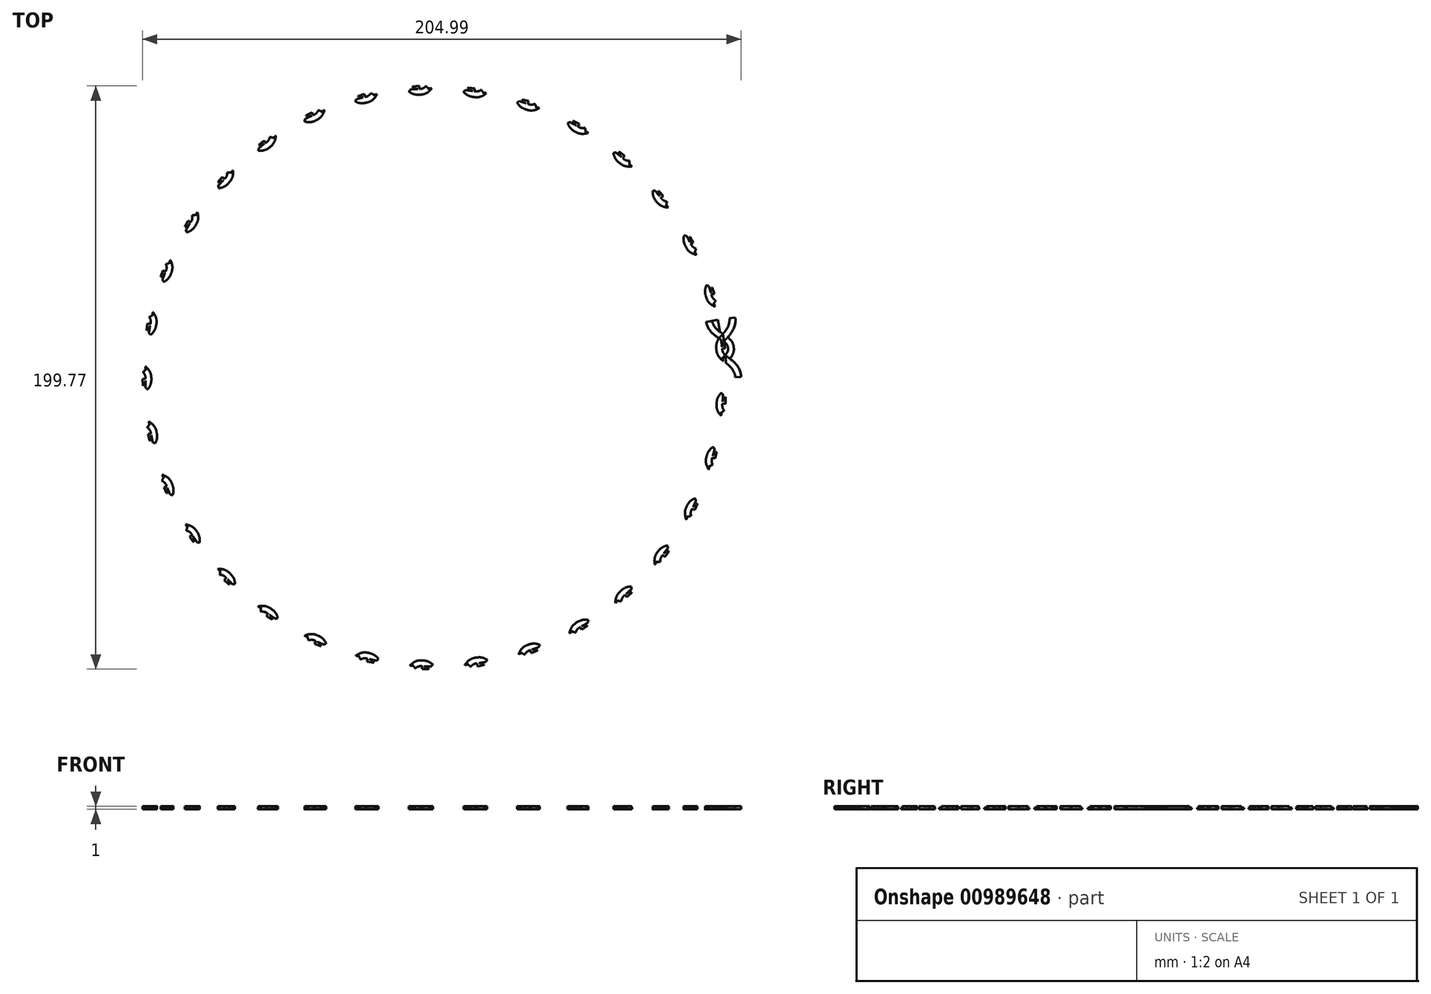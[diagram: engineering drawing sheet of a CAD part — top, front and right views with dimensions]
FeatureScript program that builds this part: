
annotation { "Feature Type Name" : "Feature", "Feature Type Description" : "" }
export const myFeature = defineFeature(function(context is Context, id is Id, definition is map)
    precondition{}
    {
        {
            var Q0;
            Q0=qCreatedBy(makeId("Top.planeOp"),FACE);
            var sketch = newSketch(context, id + "F0", { "sketchPlane" : qUnion([Q0])});
            skCircle(sketch, "E0.0", {"center": v(0.06, -0.4) * mm, "radius": 101 * mm});
            skCircle(sketch, "E1.0", {"center": v(0, 0) * mm, "radius": 99 * mm});
            skLineSegment(sketch, "E2", {"start": v(100, 0) * mm, "end": v(99.75, 5) * mm});
            skLineSegment(sketch, "E3", {"start": v(100, 0) * mm, "end": v(97, -0.15) * mm});
            skLineSegment(sketch, "E4", {"start": v(100, 0) * mm, "end": v(103, 0.15) * mm});
            skLineSegment(sketch, "E5", {"start": v(99.5, 9.99) * mm, "end": v(96.52, 9.69) * mm});
            skLineSegment(sketch, "E6", {"start": v(99.5, 9.99) * mm, "end": v(102.49, 10.29) * mm});
            skFitSpline(sketch, "E7", {"points": [v(102.49, 10.29) * mm, v(99.75, 5) * mm, v(97, -0.15) * mm], "startDerivative": vector(1.73, -14.4) * mm, "endDerivative": vector(0.3, -13.17) * mm});
            skLineSegment(sketch, "E8", {"start": v(99.5, 9.99) * mm, "end": v(100, 0) * mm});
            skPoint(sketch, "E9", {"position": v(99.6, 7.89) * mm});
            skPoint(sketch, "E10", {"position": v(99.89, 2.2) * mm});
            skLineSegment(sketch, "E11", {"start": v(99.75, 5) * mm, "end": v(99.5, 9.99) * mm});
            skFitSpline(sketch, "E12.0", {"points": [v(100.5, 10.05) * mm, v(100.52, 9.86) * mm, v(100.53, 9.55) * mm, v(100.46, 9.15) * mm, v(100.33, 8.78) * mm, v(100.11, 8.38) * mm, v(99.8, 7.95) * mm, v(99.4, 7.48) * mm, v(98.9, 6.98) * mm, v(98.36, 6.44) * mm, v(97.79, 5.85) * mm, v(97.02, 5.02) * mm, v(96.27, 4.06) * mm, v(95.65, 2.92) * mm, v(95.15, 1.66) * mm, v(94.99, 0.57) * mm, v(95, -0.2) * mm]});
            skFitSpline(sketch, "E13", {"points": [v(96.52, 9.69) * mm, v(99.75, 5) * mm, v(103, 0.15) * mm], "startDerivative": vector(1.05, -15.9) * mm, "endDerivative": vector(1.59, -14.28) * mm});
            skFitSpline(sketch, "E14.0", {"points": [v(98.51, 9.82) * mm, v(98.53, 9.58) * mm, v(98.59, 9.18) * mm, v(98.73, 8.73) * mm, v(98.91, 8.38) * mm, v(99.15, 8.06) * mm, v(99.47, 7.73) * mm, v(99.88, 7.39) * mm, v(100.38, 7) * mm, v(100.97, 6.59) * mm, v(101.59, 6.1) * mm, v(102.22, 5.57) * mm, v(102.85, 4.96) * mm, v(103.66, 4.03) * mm, v(104.52, 2.58) * mm, v(104.9, 1.14) * mm, v(104.98, 0.37) * mm]});
            skFitSpline(sketch, "E15.MirrorCS", {"points": [v(96.52, 9.69) * mm, v(98.75, 14.93) * mm, v(100.97, 20.32) * mm], "startDerivative": vector(-2.13, 15.8) * mm, "endDerivative": vector(-1.28, 14.3) * mm});
            skFitSpline(sketch, "E16.MirrorCS", {"points": [v(102.49, 10.29) * mm, v(98.75, 14.93) * mm, v(95.04, 19.43) * mm], "startDerivative": vector(-1.17, 14.46) * mm, "endDerivative": vector(-2.33, 12.96) * mm});
            skFitSpline(sketch, "E17.0", {"points": [v(100.5, 10.13) * mm, v(100.48, 10.31) * mm, v(100.42, 10.62) * mm, v(100.28, 11) * mm, v(100.07, 11.34) * mm, v(99.78, 11.68) * mm, v(99.39, 12.05) * mm, v(98.9, 12.42) * mm, v(98.32, 12.82) * mm, v(97.68, 13.24) * mm, v(97, 13.7) * mm, v(96.08, 14.37) * mm, v(95.16, 15.15) * mm, v(94.32, 16.14) * mm, v(93.58, 17.29) * mm, v(93.2, 18.32) * mm, v(93.07, 19.07) * mm]});
            skFitSpline(sketch, "E18.0", {"points": [v(98.5, 9.96) * mm, v(98.47, 10.2) * mm, v(98.44, 10.6) * mm, v(98.5, 11.06) * mm, v(98.6, 11.44) * mm, v(98.77, 11.8) * mm, v(99.02, 12.19) * mm, v(99.36, 12.61) * mm, v(99.77, 13.08) * mm, v(100.26, 13.61) * mm, v(100.78, 14.2) * mm, v(101.3, 14.85) * mm, v(101.79, 15.58) * mm, v(102.39, 16.66) * mm, v(102.95, 18.24) * mm, v(103.03, 19.73) * mm, v(102.96, 20.5) * mm]});
            skLineSegment(sketch, "E19", {"start": v(97, -0.15) * mm, "end": v(95, -0.25) * mm});
            skLineSegment(sketch, "E20", {"start": v(103, 0.15) * mm, "end": v(105, 0.25) * mm});
            skLineSegment(sketch, "E21", {"start": v(95, 0.02) * mm, "end": v(95, -0.25) * mm});
            skLineSegment(sketch, "E22", {"start": v(104.98, 0.37) * mm, "end": v(105, 0.25) * mm});
            skCircle(sketch, "E23", {"center": v(0.06, -0.4) * mm, "radius": 100 * mm, "construction": true});
            skLineSegment(sketch, "E24", {"start": v(99.5, 9.99) * mm, "end": v(97.99, 19.87) * mm});
            skLineSegment(sketch, "E25", {"start": v(100.97, 20.32) * mm, "end": v(95.04, 19.43) * mm});
            skLineSegment(sketch, "E26", {"start": v(95.04, 19.43) * mm, "end": v(93.07, 19.07) * mm});
            skLineSegment(sketch, "E27", {"start": v(100.97, 20.32) * mm, "end": v(102.96, 20.5) * mm});
            skLineSegment(sketch, "E28", {"start": v(100.5, 10.13) * mm, "end": v(100.5, 10.01) * mm});
            skSolve(sketch);
        }
        {
            var Q0;
            {var subQ0=sQuery(id+"F0.wireOp",EDGE,"E16.MirrorCS");var subQ1=sQuery(id+"F0.wireOp",EDGE,"E0.0");var subQ2=makeQuery(id+"F0.imprint","INTERSECT",VERTEX,{"derivedFrom":[subQ1,subQ0]});Q0=makeQuery(id+"F0.imprint","IMPRINT",FACE,{"disambiguationData":[TD([[makeQuery(id+"F0.imprint","IMPRINT",EDGE,{"disambiguationData":[TD([[subQ2,-1.0]])],"derivedFrom":subQ1}),1.0]])]});}
            var Q1;
            {var subQ5=sQuery(id+"F0.wireOp",EDGE,"E27");Q1=makeQuery(id+"F0.imprint","IMPRINT",FACE,{"disambiguationData":[TD([[makeQuery(id+"F0.imprint","IMPRINT",EDGE,{"derivedFrom":subQ5}),-1.0]])]});}
            var Q2;
            {var subQ0=sQuery(id+"F0.wireOp",EDGE,"E18.0");var subQ1=sQuery(id+"F0.wireOp",EDGE,"E0.0");var subQ2=makeQuery(id+"F0.imprint","INTERSECT",VERTEX,{"derivedFrom":[subQ1,subQ0]});Q2=makeQuery(id+"F0.imprint","IMPRINT",FACE,{"disambiguationData":[TD([[makeQuery(id+"F0.imprint","IMPRINT",EDGE,{"disambiguationData":[TD([[subQ2,-1.0]])],"derivedFrom":subQ1}),1.0]])]});}
            var Q3;
            {var subQ1=sQuery(id+"F0.wireOp",EDGE,"E1.0");var subQ5=sQuery(id+"F0.wireOp",EDGE,"E15.MirrorCS");var subQ6=makeQuery(id+"F0.imprint","INTERSECT",VERTEX,{"derivedFrom":[subQ1,subQ5]});Q3=makeQuery(id+"F0.imprint","IMPRINT",FACE,{"disambiguationData":[TD([[makeQuery(id+"F0.imprint","IMPRINT",EDGE,{"disambiguationData":[TD([[subQ6,-1.0]])],"derivedFrom":subQ1}),1.0]])]});}
            var Q4;
            {var subQ0=sQuery(id+"F0.wireOp",EDGE,"E15.MirrorCS");var subQ1=sQuery(id+"F0.wireOp",EDGE,"E1.0");var subQ2=makeQuery(id+"F0.imprint","INTERSECT",VERTEX,{"derivedFrom":[subQ1,subQ0]});Q4=makeQuery(id+"F0.imprint","IMPRINT",FACE,{"disambiguationData":[TD([[makeQuery(id+"F0.imprint","IMPRINT",EDGE,{"disambiguationData":[TD([[subQ2,-1.0]])],"derivedFrom":subQ1}),-1.0]])]});}
            var Q5;
            {var subQ0=sQuery(id+"F0.wireOp",EDGE,"E18.0");var subQ1=sQuery(id+"F0.wireOp",EDGE,"E0.0");var subQ2=makeQuery(id+"F0.imprint","INTERSECT",VERTEX,{"derivedFrom":[subQ1,subQ0]});Q5=makeQuery(id+"F0.imprint","IMPRINT",FACE,{"disambiguationData":[TD([[makeQuery(id+"F0.imprint","IMPRINT",EDGE,{"disambiguationData":[TD([[subQ2,-1.0]])],"derivedFrom":subQ1}),-1.0]])]});}
            var Q6;
            {var subQ5=sQuery(id+"F0.wireOp",EDGE,"E1.0");var subQ7=makeQuery(id+"F0.imprint","INTERSECT",VERTEX,{"derivedFrom":[subQ5,sQuery(id+"F0.wireOp",EDGE,"E18.0")]});Q6=makeQuery(id+"F0.imprint","IMPRINT",FACE,{"disambiguationData":[TD([[makeQuery(id+"F0.imprint","IMPRINT",EDGE,{"disambiguationData":[TD([[subQ7,1.0]])],"derivedFrom":subQ5}),-1.0]])]});}
            var Q7;
            {var subQ0=sQuery(id+"F0.wireOp",EDGE,"E18.0");var subQ1=sQuery(id+"F0.wireOp",EDGE,"E1.0");var subQ2=makeQuery(id+"F0.imprint","INTERSECT",VERTEX,{"derivedFrom":[subQ1,subQ0]});Q7=makeQuery(id+"F0.imprint","IMPRINT",FACE,{"disambiguationData":[TD([[makeQuery(id+"F0.imprint","IMPRINT",EDGE,{"disambiguationData":[TD([[subQ2,1.0]])],"derivedFrom":subQ1}),1.0]])]});}
            var Q8;
            {var subQ0=sQuery(id+"F0.wireOp",EDGE,"E7");var subQ1=sQuery(id+"F0.wireOp",EDGE,"E0.0");var subQ2=makeQuery(id+"F0.imprint","INTERSECT",VERTEX,{"derivedFrom":[subQ1,subQ0]});Q8=makeQuery(id+"F0.imprint","IMPRINT",FACE,{"disambiguationData":[TD([[makeQuery(id+"F0.imprint","IMPRINT",EDGE,{"disambiguationData":[TD([[subQ2,-1.0]])],"derivedFrom":subQ1}),1.0]])]});}
            var Q9;
            {var subQ0=sQuery(id+"F0.wireOp",EDGE,"E7");var subQ1=sQuery(id+"F0.wireOp",EDGE,"E0.0");var subQ2=makeQuery(id+"F0.imprint","INTERSECT",VERTEX,{"derivedFrom":[subQ1,subQ0]});Q9=makeQuery(id+"F0.imprint","IMPRINT",FACE,{"disambiguationData":[TD([[makeQuery(id+"F0.imprint","IMPRINT",EDGE,{"disambiguationData":[TD([[subQ2,-1.0]])],"derivedFrom":subQ1}),-1.0]])]});}
            var Q10;
            {var subQ3=sQuery(id+"F0.wireOp",EDGE,"E1.0");var subQ5=sQuery(id+"F0.wireOp",EDGE,"E12.0");var subQ6=makeQuery(id+"F0.imprint","INTERSECT",VERTEX,{"derivedFrom":[subQ3,subQ5]});Q10=makeQuery(id+"F0.imprint","IMPRINT",FACE,{"disambiguationData":[TD([[makeQuery(id+"F0.imprint","IMPRINT",EDGE,{"disambiguationData":[TD([[subQ6,-1.0]])],"derivedFrom":subQ3}),1.0]])]});}
            var Q11;
            {var subQ0=sQuery(id+"F0.wireOp",EDGE,"E12.0");var subQ1=sQuery(id+"F0.wireOp",EDGE,"E1.0");var subQ2=makeQuery(id+"F0.imprint","INTERSECT",VERTEX,{"derivedFrom":[subQ1,subQ0]});Q11=makeQuery(id+"F0.imprint","IMPRINT",FACE,{"disambiguationData":[TD([[makeQuery(id+"F0.imprint","IMPRINT",EDGE,{"disambiguationData":[TD([[subQ2,-1.0]])],"derivedFrom":subQ1}),-1.0]])]});}
            var Q12;
            {var subQ1=sQuery(id+"F0.wireOp",EDGE,"E1.0");var subQ5=makeQuery(id+"F0.imprint","INTERSECT",VERTEX,{"derivedFrom":[subQ1,sQuery(id+"F0.wireOp",EDGE,"E14.0")]});Q12=makeQuery(id+"F0.imprint","IMPRINT",FACE,{"disambiguationData":[TD([[makeQuery(id+"F0.imprint","IMPRINT",EDGE,{"disambiguationData":[TD([[subQ5,1.0]])],"derivedFrom":subQ1}),-1.0]])]});}
            var Q13;
            {var subQ0=sQuery(id+"F0.wireOp",EDGE,"E14.0");var subQ1=sQuery(id+"F0.wireOp",EDGE,"E1.0");var subQ2=makeQuery(id+"F0.imprint","INTERSECT",VERTEX,{"derivedFrom":[subQ1,subQ0]});Q13=makeQuery(id+"F0.imprint","IMPRINT",FACE,{"disambiguationData":[TD([[makeQuery(id+"F0.imprint","IMPRINT",EDGE,{"disambiguationData":[TD([[subQ2,-1.0]])],"derivedFrom":subQ1}),1.0]])]});}
            var Q14;
            {var subQ0=sQuery(id+"F0.wireOp",EDGE,"E13");var subQ1=sQuery(id+"F0.wireOp",EDGE,"E0.0");var subQ2=makeQuery(id+"F0.imprint","INTERSECT",VERTEX,{"derivedFrom":[subQ1,subQ0]});Q14=makeQuery(id+"F0.imprint","IMPRINT",FACE,{"disambiguationData":[TD([[makeQuery(id+"F0.imprint","IMPRINT",EDGE,{"disambiguationData":[TD([[subQ2,-1.0]])],"derivedFrom":subQ1}),1.0]])]});}
            var Q15;
            {var subQ4=sQuery(id+"F0.wireOp",EDGE,"E20");Q15=makeQuery(id+"F0.imprint","IMPRINT",FACE,{"disambiguationData":[TD([[makeQuery(id+"F0.imprint","IMPRINT",EDGE,{"derivedFrom":subQ4}),1.0]])]});}
            extrude(context, id + "F1", {"entities" : qUnion([Q0, Q1, Q2, Q3, Q4, Q5, Q6, Q7, Q8, Q9, Q10, Q11, Q12, Q13, Q14, Q15]), "depth" : 1 * mm, "offsetDistance" : 25 * mm});
        }
        {
            var Q0;
            {var subQ5=sQuery(id+"F0.wireOp",EDGE,"E19");Q0=makeQuery(id+"F0.imprint","IMPRINT",FACE,{"disambiguationData":[TD([[makeQuery(id+"F0.imprint","IMPRINT",EDGE,{"derivedFrom":subQ5}),-1.0]])]});}
            var Q1;
            {var subQ0=sQuery(id+"F0.wireOp",EDGE,"E13");var subQ1=sQuery(id+"F0.wireOp",EDGE,"E1.0");var subQ2=makeQuery(id+"F0.imprint","INTERSECT",VERTEX,{"derivedFrom":[subQ1,subQ0]});Q1=makeQuery(id+"F0.imprint","IMPRINT",FACE,{"disambiguationData":[TD([[makeQuery(id+"F0.imprint","IMPRINT",EDGE,{"disambiguationData":[TD([[subQ2,-1.0]])],"derivedFrom":subQ1}),1.0]])]});}
            var Q2;
            {var subQ0=sQuery(id+"F0.wireOp",EDGE,"E14.0");var subQ5=sQuery(id+"F0.wireOp",EDGE,"E0.0");var subQ6=makeQuery(id+"F0.imprint","INTERSECT",VERTEX,{"derivedFrom":[subQ5,subQ0]});Q2=makeQuery(id+"F0.imprint","IMPRINT",FACE,{"disambiguationData":[TD([[makeQuery(id+"F0.imprint","IMPRINT",EDGE,{"disambiguationData":[TD([[subQ6,-1.0]])],"derivedFrom":subQ5}),1.0]])]});}
            var Q3;
            {var subQ0=sQuery(id+"F0.wireOp",EDGE,"E6");var subQ1=sQuery(id+"F0.wireOp",EDGE,"E0.0");var subQ2=makeQuery(id+"F0.imprint","INTERSECT",VERTEX,{"derivedFrom":[subQ1,subQ0]});Q3=makeQuery(id+"F0.imprint","IMPRINT",FACE,{"disambiguationData":[TD([[makeQuery(id+"F0.imprint","IMPRINT",EDGE,{"disambiguationData":[TD([[subQ2,-1.0]])],"derivedFrom":subQ1}),-1.0]])]});}
            var Q4;
            {var subQ6=sQuery(id+"F0.wireOp",EDGE,"E0.0");var subQ9=sQuery(id+"F0.wireOp",EDGE,"E6");var subQ10=makeQuery(id+"F0.imprint","INTERSECT",VERTEX,{"derivedFrom":[subQ6,subQ9]});Q4=makeQuery(id+"F0.imprint","IMPRINT",FACE,{"disambiguationData":[TD([[makeQuery(id+"F0.imprint","IMPRINT",EDGE,{"disambiguationData":[TD([[subQ10,-1.0]])],"derivedFrom":subQ6}),1.0]])]});}
            var Q5;
            {var subQ0=sQuery(id+"F0.wireOp",EDGE,"E14.0");var subQ1=sQuery(id+"F0.wireOp",EDGE,"E0.0");var subQ2=makeQuery(id+"F0.imprint","INTERSECT",VERTEX,{"derivedFrom":[subQ1,subQ0]});Q5=makeQuery(id+"F0.imprint","IMPRINT",FACE,{"disambiguationData":[TD([[makeQuery(id+"F0.imprint","IMPRINT",EDGE,{"disambiguationData":[TD([[subQ2,-1.0]])],"derivedFrom":subQ1}),-1.0]])]});}
            var Q6;
            {var subQ0=sQuery(id+"F0.wireOp",EDGE,"E26");Q6=makeQuery(id+"F0.imprint","IMPRINT",FACE,{"disambiguationData":[TD([[makeQuery(id+"F0.imprint","IMPRINT",EDGE,{"derivedFrom":subQ0}),1.0]])]});}
            var Q7;
            {var subQ0=sQuery(id+"F0.wireOp",EDGE,"E16.MirrorCS");var subQ1=sQuery(id+"F0.wireOp",EDGE,"E1.0");var subQ2=makeQuery(id+"F0.imprint","INTERSECT",VERTEX,{"derivedFrom":[subQ1,subQ0]});Q7=makeQuery(id+"F0.imprint","IMPRINT",FACE,{"disambiguationData":[TD([[makeQuery(id+"F0.imprint","IMPRINT",EDGE,{"disambiguationData":[TD([[subQ2,-1.0]])],"derivedFrom":subQ1}),1.0]])]});}
            extrude(context, id + "F2", {"entities" : qUnion([Q0, Q1, Q2, Q3, Q4, Q5, Q6, Q7]), "operationType" : NewBodyOperationType.ADD, "depth" : 0.5 * mm, "offsetDistance" : 25 * mm});
        }
        {
            var Q0;
            Q0=qCreatedBy(makeId("Front.planeOp"),FACE);
            var sketch = newSketch(context, id + "F3", { "sketchPlane" : qUnion([Q0])});
            skLineSegment(sketch, "E29", {"start": v(0, 24.91) * mm, "end": v(0, -16.52) * mm, "construction": true});
            skSolve(sketch);
        }
        {
            var Q0;
            Q0=makeQuery(id+"F1.opExtrude","SWEPT_BODY",BODY,{"disambiguationData":[OSD([sQuery(id+"F0.wireOp",EDGE,"E1.0"),sQuery(id+"F0.wireOp",EDGE,"E7"),sQuery(id+"F0.wireOp",EDGE,"E11"),sQuery(id+"F0.wireOp",EDGE,"E12.0"),sQuery(id+"F0.wireOp",EDGE,"E13"),sQuery(id+"F0.wireOp",EDGE,"E14.0"),sQuery(id+"F0.wireOp",EDGE,"E15.MirrorCS"),sQuery(id+"F0.wireOp",EDGE,"E16.MirrorCS"),sQuery(id+"F0.wireOp",EDGE,"E17.0"),sQuery(id+"F0.wireOp",EDGE,"E18.0"),sQuery(id+"F0.wireOp",EDGE,"E19"),sQuery(id+"F0.wireOp",EDGE,"E20"),sQuery(id+"F0.wireOp",EDGE,"E21"),sQuery(id+"F0.wireOp",EDGE,"E22"),sQuery(id+"F0.wireOp",EDGE,"E24"),sQuery(id+"F0.wireOp",EDGE,"E26"),sQuery(id+"F0.wireOp",EDGE,"E27"),sQuery(id+"F0.wireOp",EDGE,"E28")])]});
            var Q1;
            Q1=sQuery(id+"F3.wireOp",EDGE,"E29");
            circularPattern(context, id + "F4", {"operationType" : NewBodyOperationType.ADD, "entities" : qUnion([Q0]), "axis" : qUnion([Q1]), "angle" : 360 * degree, "instanceCount" : 33, "equalSpace" : true});
        }
    });
